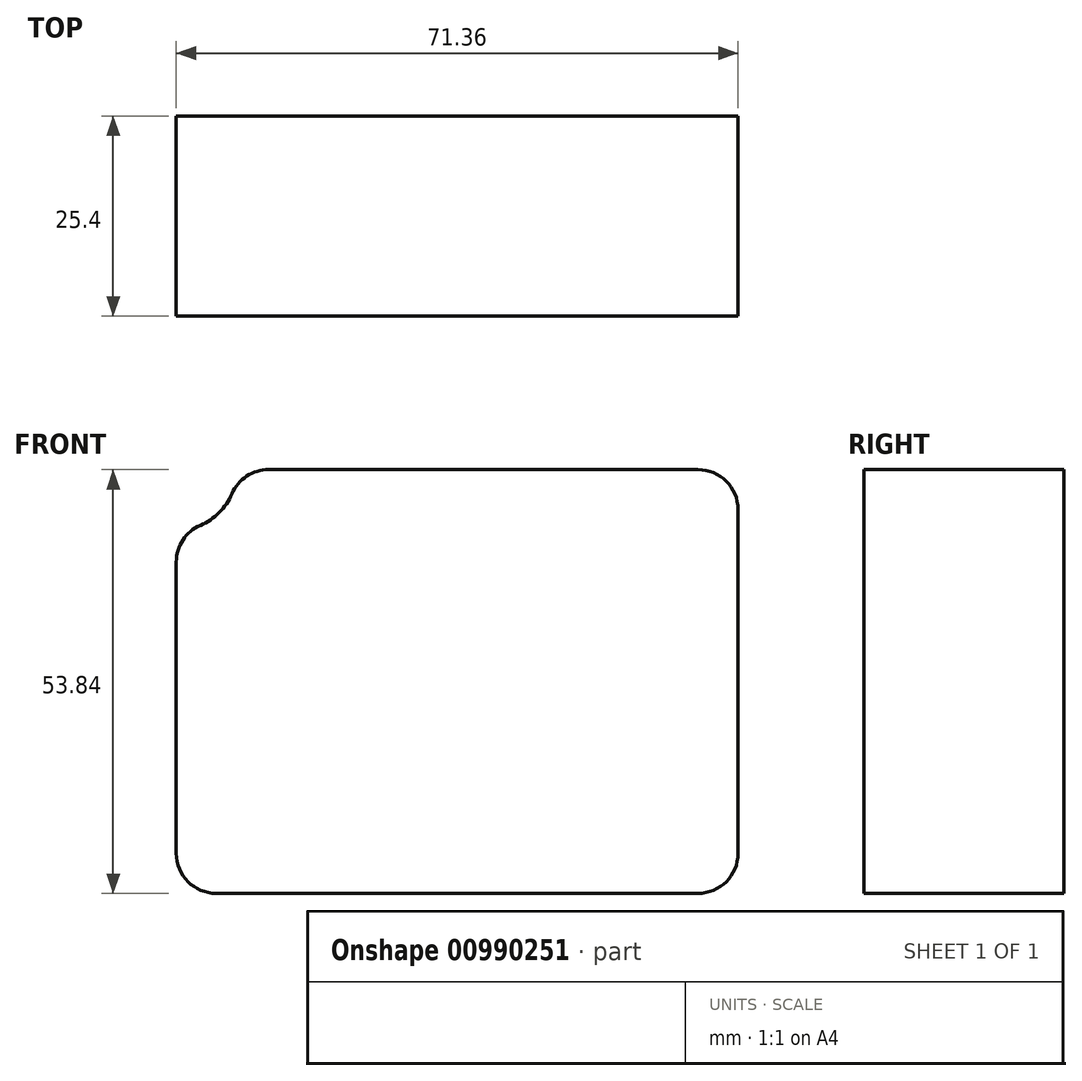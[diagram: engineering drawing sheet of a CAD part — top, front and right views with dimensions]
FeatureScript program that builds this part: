
annotation { "Feature Type Name" : "Feature", "Feature Type Description" : "" }
export const myFeature = defineFeature(function(context is Context, id is Id, definition is map)
    precondition{}
    {
        {
            var Q0;
            Q0=qCreatedBy(makeId("Front.planeOp"),FACE);
            var sketch = newSketch(context, id + "F0", { "sketchPlane" : qUnion([Q0])});
            skLineSegment(sketch, "E0.bottom", {"start": v(35.68, -26.92) * mm, "end": v(-35.68, -26.92) * mm});
            skLineSegment(sketch, "E0.top", {"start": v(35.68, 26.92) * mm, "end": v(-35.68, 26.92) * mm});
            skLineSegment(sketch, "E0.left", {"start": v(35.68, -26.92) * mm, "end": v(35.68, 26.92) * mm});
            skLineSegment(sketch, "E0.right", {"start": v(-35.68, -26.92) * mm, "end": v(-35.68, 26.92) * mm});
            skPoint(sketch, "E0.middle", {"position": v(0, 0) * mm});
            skLineSegment(sketch, "E1", {"start": v(-35.68, 26.92) * mm, "end": v(35.68, -26.92) * mm, "construction": true});
            skLineSegment(sketch, "E2", {"start": v(35.68, 26.92) * mm, "end": v(-35.68, -26.92) * mm, "construction": true});
            skCircle(sketch, "E3", {"center": v(-35.68, 26.92) * mm, "radius": 7.71 * mm});
            skSolve(sketch);
        }
        {
            var Q0;
            Q0=makeQuery(id+"F0.imprint","IMPRINT",FACE,{"disambiguationData":[TD([[makeQuery(id+"F0.imprint","IMPRINT",EDGE,{"derivedFrom":sQuery(id+"F0.wireOp",EDGE,"E0.bottom")}),-1.0]])]});
            extrude(context, id + "F1", {"entities" : qUnion([Q0]), "depth" : 25.4 * mm, "offsetDistance" : 25.4 * mm});
        }
        {
            var Q0;
            Q0=makeQuery(id+"F1.opExtrude","SWEPT_EDGE",EDGE,{"disambiguationData":[OSD([sQuery(id+"F0.wireOp",EDGE,"E0.top"),sQuery(id+"F0.wireOp",EDGE,"E0.left")])]});
            var Q1;
            Q1=makeQuery(id+"F1.opExtrude","SWEPT_EDGE",EDGE,{"disambiguationData":[OSD([sQuery(id+"F0.wireOp",EDGE,"E0.top"),sQuery(id+"F0.wireOp",EDGE,"E0.right")])]});
            var Q2;
            Q2=makeQuery(id+"F1.opExtrude","SWEPT_EDGE",EDGE,{"disambiguationData":[OSD([sQuery(id+"F0.wireOp",EDGE,"E0.bottom"),sQuery(id+"F0.wireOp",EDGE,"E0.right")])]});
            var Q3;
            Q3=makeQuery(id+"F1.opExtrude","SWEPT_EDGE",EDGE,{"disambiguationData":[OSD([sQuery(id+"F0.wireOp",EDGE,"E0.bottom"),sQuery(id+"F0.wireOp",EDGE,"E0.left")])]});
            fillet(context, id + "F2", {"entities" : qUnion([Q0, Q1, Q2, Q3]), "radius" : 5.08 * mm, "tangentPropagation" : true, "allowEdgeOverflow" : false});
        }
    });
